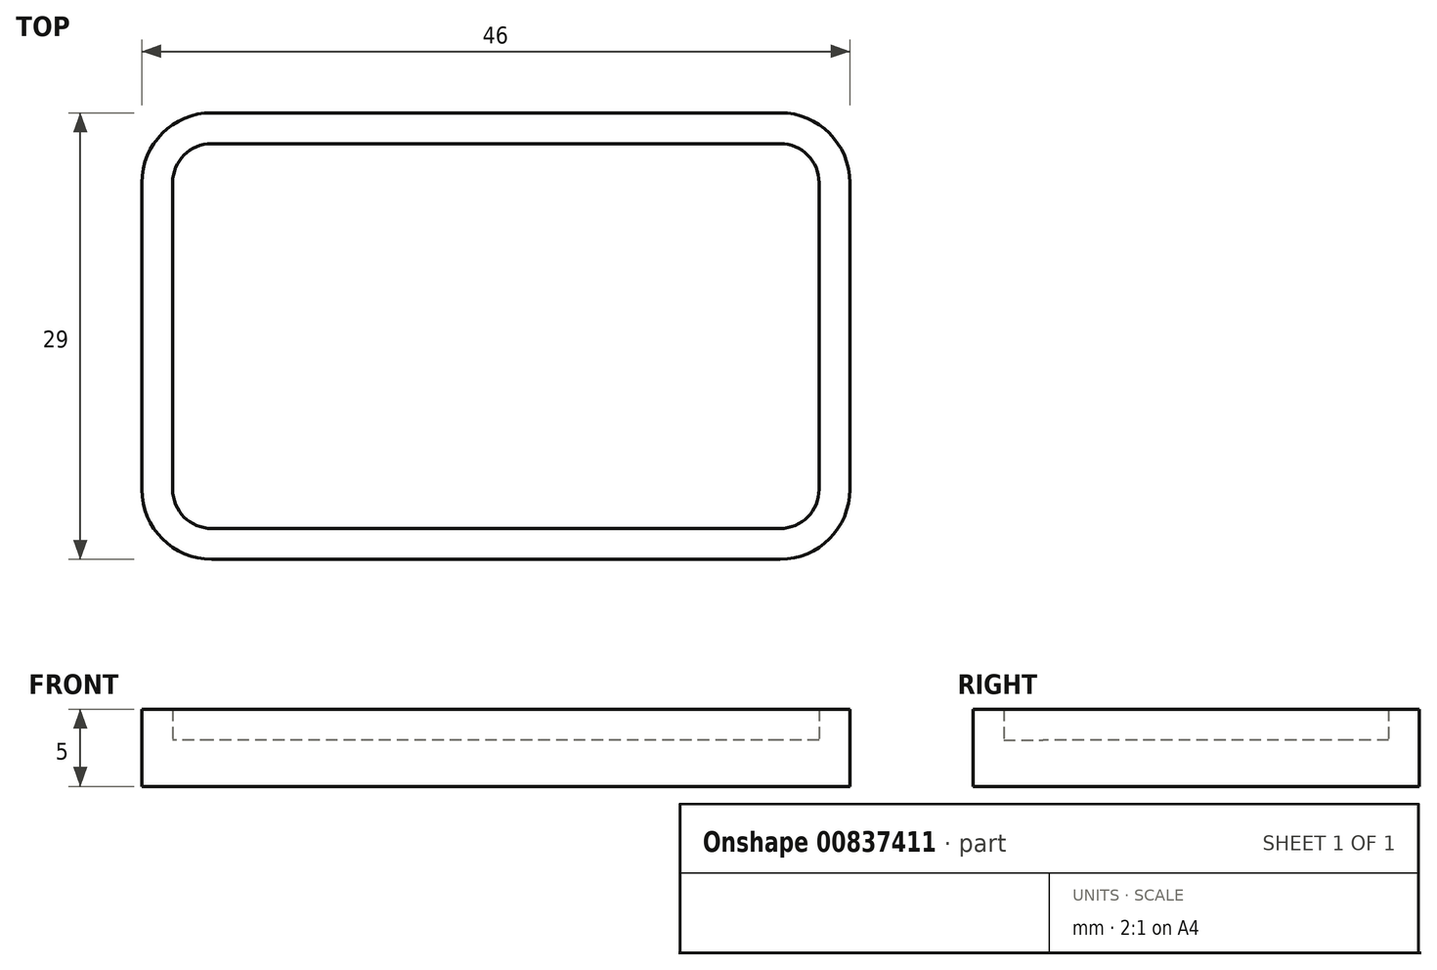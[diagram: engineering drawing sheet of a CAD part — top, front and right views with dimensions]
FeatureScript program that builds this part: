
annotation { "Feature Type Name" : "Feature", "Feature Type Description" : "" }
export const myFeature = defineFeature(function(context is Context, id is Id, definition is map)
    precondition{}
    {
        {
            var Q0;
            Q0=qCreatedBy(makeId("Top.planeOp"),FACE);
            var sketch = newSketch(context, id + "F0", { "sketchPlane" : qUnion([Q0])});
            skLineSegment(sketch, "E0.bottom", {"start": v(18.46, 12.5) * mm, "end": v(-18.46, 12.5) * mm});
            skLineSegment(sketch, "E0.top", {"start": v(18.46, -12.5) * mm, "end": v(-18.46, -12.5) * mm});
            skLineSegment(sketch, "E0.left", {"start": v(21, 9.96) * mm, "end": v(21, -9.96) * mm});
            skLineSegment(sketch, "E0.right", {"start": v(-21, 9.96) * mm, "end": v(-21, -9.96) * mm});
            skPoint(sketch, "E0.middle", {"position": v(0, 0) * mm});
            skPoint(sketch, "E1.visualSharp", {"position": v(-21, 12.5) * mm});
            skArc(sketch, "E1.filletArc", {"start": v(-18.46, 12.5) * mm, "mid": v(-20.26, 11.76) * mm, "end": v(-21, 9.96) * mm});
            skPoint(sketch, "E2.visualSharp", {"position": v(-21, -12.5) * mm});
            skArc(sketch, "E2.filletArc", {"start": v(-21, -9.96) * mm, "mid": v(-20.26, -11.76) * mm, "end": v(-18.46, -12.5) * mm});
            skPoint(sketch, "E3.visualSharp", {"position": v(21, -12.5) * mm});
            skArc(sketch, "E3.filletArc", {"start": v(18.46, -12.5) * mm, "mid": v(20.26, -11.76) * mm, "end": v(21, -9.96) * mm});
            skPoint(sketch, "E4.visualSharp", {"position": v(21, 12.5) * mm});
            skArc(sketch, "E4.filletArc", {"start": v(21, 9.96) * mm, "mid": v(20.26, 11.76) * mm, "end": v(18.46, 12.5) * mm});
            skSolve(sketch);
        }
        {
            var Q0;
            Q0=makeQuery(id+"F0.imprint","IMPRINT",FACE,{"disambiguationData":[TD([[makeQuery(id+"F0.imprint","IMPRINT",EDGE,{"derivedFrom":sQuery(id+"F0.wireOp",EDGE,"E0.bottom")}),1.0]])]});
            var sketch = newSketch(context, id + "F1", { "sketchPlane" : qUnion([Q0])});
            skLineSegment(sketch, "E5.0", {"start": v(18.46, 14.5) * mm, "end": v(-18.46, 14.5) * mm});
            skArc(sketch, "E6.0", {"start": v(23, 9.96) * mm, "mid": v(21.67, 13.17) * mm, "end": v(18.46, 14.5) * mm});
            skLineSegment(sketch, "E6.1", {"start": v(23, 9.96) * mm, "end": v(23, -9.96) * mm});
            skArc(sketch, "E6.2", {"start": v(18.46, -14.5) * mm, "mid": v(21.67, -13.17) * mm, "end": v(23, -9.96) * mm});
            skArc(sketch, "E6.3", {"start": v(-18.46, 14.5) * mm, "mid": v(-21.67, 13.17) * mm, "end": v(-23, 9.96) * mm});
            skLineSegment(sketch, "E6.4", {"start": v(-23, 9.96) * mm, "end": v(-23, -9.96) * mm});
            skArc(sketch, "E6.5", {"start": v(-23, -9.96) * mm, "mid": v(-21.67, -13.17) * mm, "end": v(-18.46, -14.5) * mm});
            skLineSegment(sketch, "E6.6", {"start": v(18.46, -14.5) * mm, "end": v(-18.46, -14.5) * mm});
            skSolve(sketch);
        }
        {
            var Q0;
            Q0=makeQuery(id+"F0.imprint","IMPRINT",FACE,{"disambiguationData":[TD([[makeQuery(id+"F0.imprint","IMPRINT",EDGE,{"derivedFrom":sQuery(id+"F0.wireOp",EDGE,"E0.bottom")}),1.0]])]});
            extrude(context, id + "F2", {"entities" : qUnion([Q0]), "depth" : 3 * mm, "offsetDistance" : 25.4 * mm});
        }
        {
            var Q0;
            Q0=makeQuery(id+"F1.imprint","IMPRINT",FACE,{"disambiguationData":[TD([[makeQuery(id+"F1.imprint","IMPRINT",EDGE,{"derivedFrom":sQuery(id+"F1.wireOp",EDGE,"E5.0")}),1.0]])]});
            extrude(context, id + "F3", {"entities" : qUnion([Q0]), "operationType" : NewBodyOperationType.ADD, "depth" : 5 * mm, "offsetDistance" : 25.4 * mm});
        }
    });
